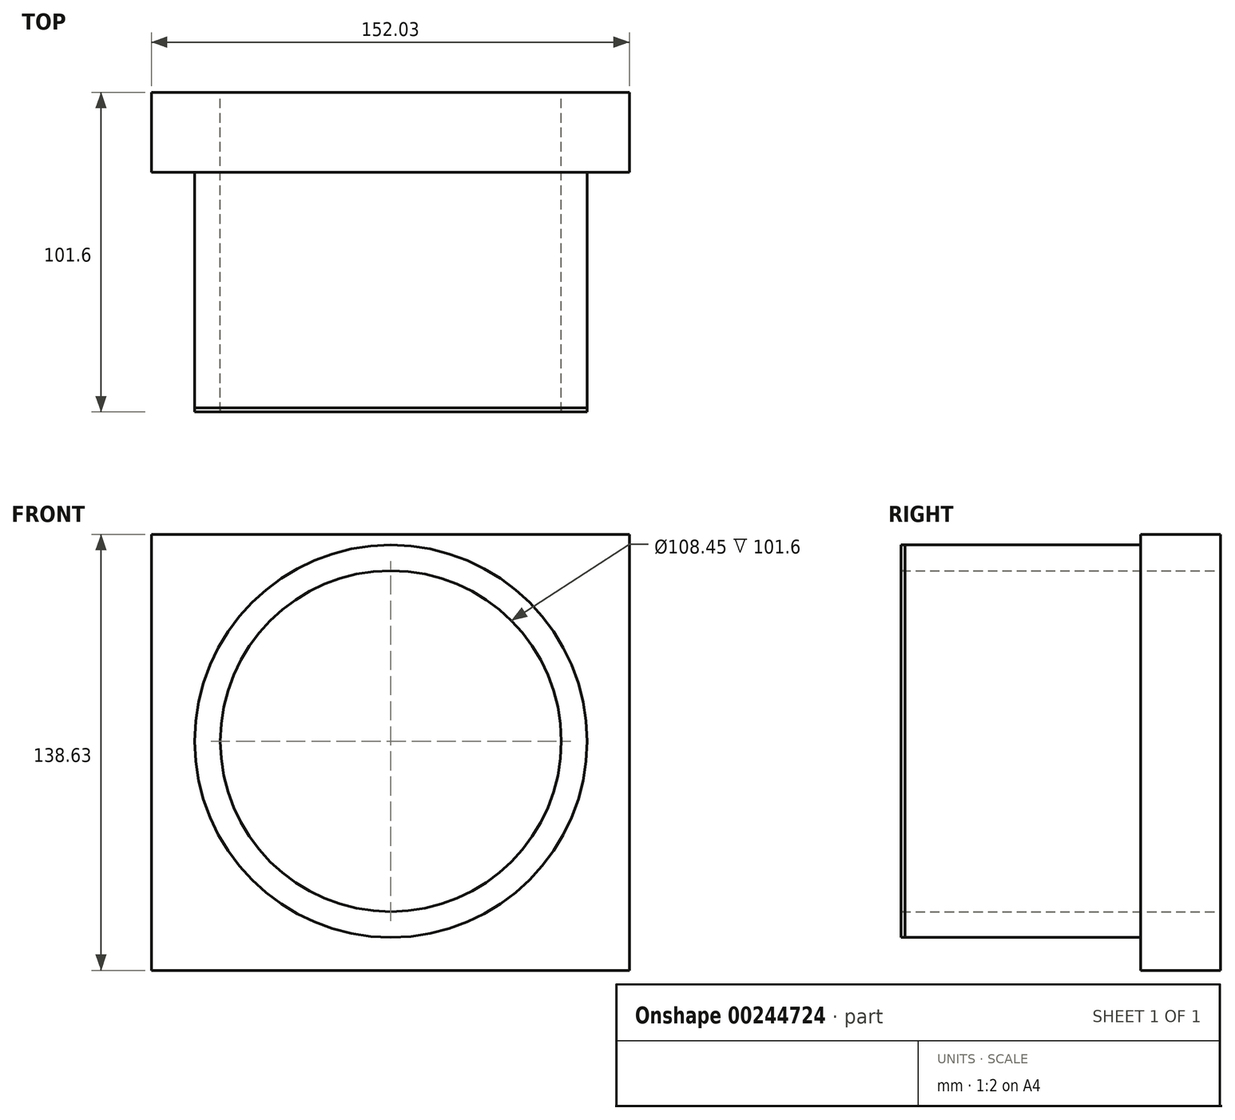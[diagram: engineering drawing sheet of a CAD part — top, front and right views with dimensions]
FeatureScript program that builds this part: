
annotation { "Feature Type Name" : "Feature", "Feature Type Description" : "" }
export const myFeature = defineFeature(function(context is Context, id is Id, definition is map)
    precondition{}
    {
        {
            var Q0;
            Q0=qCreatedBy(makeId("Front.planeOp"),FACE);
            var sketch = newSketch(context, id + "F0", { "sketchPlane" : qUnion([Q0])});
            skCircle(sketch, "E0", {"center": v(0, 0) * mm, "radius": 54.22 * mm});
            skLineSegment(sketch, "E1.bottom", {"start": v(-76.16, 65.75) * mm, "end": v(75.87, 65.75) * mm});
            skLineSegment(sketch, "E1.top", {"start": v(-76.16, -72.88) * mm, "end": v(75.87, -72.88) * mm});
            skLineSegment(sketch, "E1.left", {"start": v(-76.16, 65.75) * mm, "end": v(-76.16, -72.88) * mm});
            skLineSegment(sketch, "E1.right", {"start": v(75.87, 65.75) * mm, "end": v(75.87, -72.88) * mm});
            skCircle(sketch, "E2", {"center": v(0, 0) * mm, "radius": 62.4 * mm});
            skSolve(sketch);
        }
        {
            var Q0;
            Q0=makeQuery(id+"F0.imprint","IMPRINT",FACE,{"disambiguationData":[TD([[makeQuery(id+"F0.imprint","IMPRINT",EDGE,{"derivedFrom":sQuery(id+"F0.wireOp",EDGE,"E0")}),-1.0]])]});
            extrude(context, id + "F1", {"entities" : qUnion([Q0]), "depth" : 25.4 * mm});
        }
        {
            var Q0;
            Q0=makeQuery(id+"F1.opExtrude","CAP_FACE",FACE,{"disambiguationData":[OSD([sQuery(id+"F0.wireOp",EDGE,"E0"),sQuery(id+"F0.wireOp",EDGE,"E1.bottom"),sQuery(id+"F0.wireOp",EDGE,"E1.top"),sQuery(id+"F0.wireOp",EDGE,"E1.left"),sQuery(id+"F0.wireOp",EDGE,"E1.right")])],"isStart":false});
            var Q1;
            Q1=makeQuery(id+"F1.opExtrude","CAP_FACE",FACE,{"disambiguationData":[OSD([sQuery(id+"F0.wireOp",EDGE,"E0"),sQuery(id+"F0.wireOp",EDGE,"E1.bottom"),sQuery(id+"F0.wireOp",EDGE,"E1.top"),sQuery(id+"F0.wireOp",EDGE,"E1.left"),sQuery(id+"F0.wireOp",EDGE,"E1.right")])],"isStart":true});
            extrude(context, id + "F2", {"entities" : qUnion([Q0, Q1]), "operationType" : NewBodyOperationType.ADD, "depth" : 50.8 * mm});
        }
        {
            var Q0;
            Q0 = qSketchRegion(id + "F0", true);
            var Q1;
            {var subQ0=sQuery(id+"F0.wireOp",EDGE,"E2");var subQ1=sQuery(id+"F0.wireOp",EDGE,"E0");Q1=makeQuery(id+"F2.opExtrude","CAP_FACE",FACE,{"disambiguationData":[OSD([subQ1,subQ0]),TDD([makeQuery(id+"F1.opExtrude","CAP_FACE",FACE,{"disambiguationData":[OSD([subQ1,subQ0])],"isStart":false})])],"isStart":false});}
            extrude(context, id + "F3", {"entities" : qUnion([Q0, Q1]), "operationType" : NewBodyOperationType.ADD, "depth" : 25.4 * mm});
        }
        {
            var Q0;
            Q0=makeQuery(id+"F3.opExtrude","CAP_FACE",FACE,{"disambiguationData":[OSD([sQuery(id+"F0.wireOp",EDGE,"E0"),sQuery(id+"F0.wireOp",EDGE,"E2")])],"isStart":false});
            extrude(context, id + "F4", {"entities" : qUnion([Q0]), "oppositeDirection" : true, "depth" : 1.27 * mm});
        }
    });
